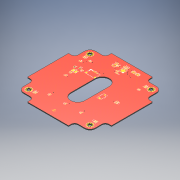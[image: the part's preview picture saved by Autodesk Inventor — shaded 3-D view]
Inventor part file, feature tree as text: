
AUTODESK INVENTOR PART (.ipt)
format: ipt  version: 2018 (Build 220112000, 112)  size: 744,448 bytes
history: native  units: mm
features: sketch x7, hole x4, other x4, extrude x1, fillet x1
ambient origin geometry x8: Origin, YZ Plane, XZ Plane, XY Plane, X Axis, Y Axis, Z Axis, Center Point
bodies: Solid1 (feature_tree)
feature tree (17):
  extrude  "Extrusion1"  Depth=96.0mm
  fillet  "Fillet1"  Radius=80.0mm
  hole  "Hole3"  [1 undecoded]
  other  "Decal3"
  other  "Decal2"
  hole  "Hole4"  [1 undecoded]
  hole  "Hole5"  [1 undecoded]
  hole  "Hole6"  [1 undecoded]
  sketch  "Sketch1"  dims[d0=96.0mm d1=96.0mm d3=80.0mm]
  sketch  "Sketch4"  dims[d5=1.0mm d6=0.0mm d7=16.0mm]
  sketch  "Sketch8"  dims[d11=0.5mm d35=70.0mm]
  other  "Image3"
  sketch  "Sketch9"  dims[d36=3.4mm d37=6.0mm d38=6.3mm d39=2.0mm d40=90.0deg d41=8.0mm d42=20.594885mm d48=90.0mm]
  sketch  "Sketch10"  dims[d49=65.0mm d50=56.0mm]
  sketch  "Sketch11"  dims[d51=93.0mm]
  sketch  "Sketch13"  dims[d52=8.0mm d53=70.0mm d54=6.0mm d55=23.5mm d56=23.5mm d57=4.0mm d58=41.0mm d59=28.0mm d66=0.7mm d67=6.0mm d68=4.0mm d69=2.0mm d70=90.0deg d71=8.0mm d72=20.594885mm d73=0.45mm d74=6.0mm d75=4.0mm d76=2.0mm d77=90.0deg d78=8.0mm d79=20.594885mm d80=0.35mm d81=6.0mm d82=4.0mm d83=2.0mm d84=90.0deg d85=8.0mm d86=20.594885mm]
  other  "Image4"
note: 4 required parameter values undecoded (feature->parameter linkage not recoverable at this tier; creation-order binding heuristic only, values carry confidence <= 0.55)
